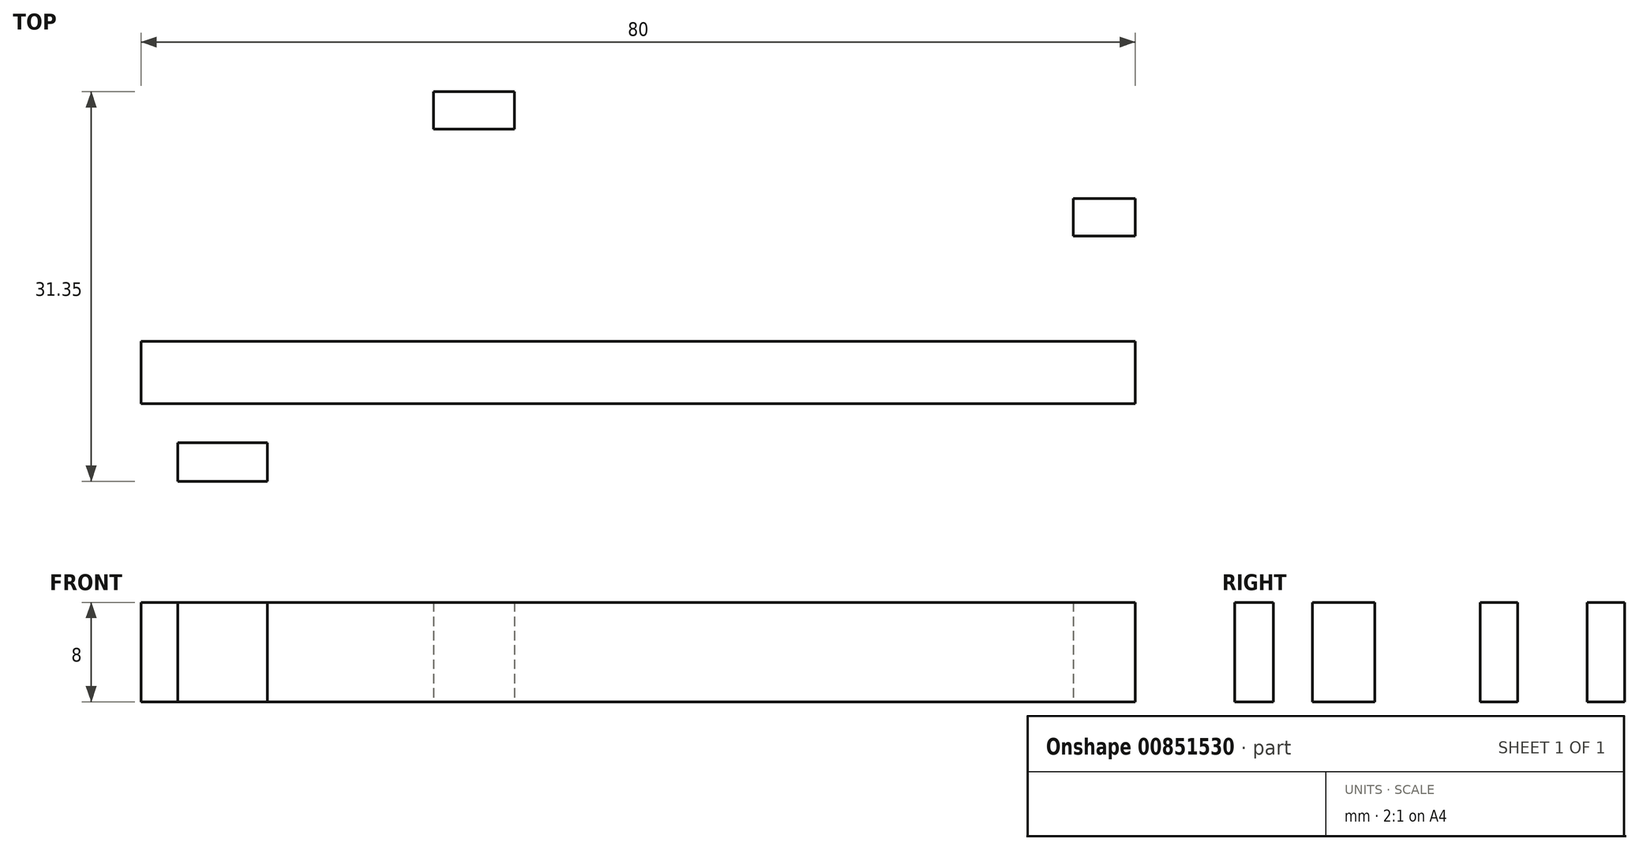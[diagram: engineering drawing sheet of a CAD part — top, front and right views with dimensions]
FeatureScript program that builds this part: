
annotation { "Feature Type Name" : "Feature", "Feature Type Description" : "" }
export const myFeature = defineFeature(function(context is Context, id is Id, definition is map)
    precondition{}
    {
        {
            var Q0;
            Q0=qCreatedBy(makeId("Top.planeOp"),FACE);
            var sketch = newSketch(context, id + "F0", { "sketchPlane" : qUnion([Q0])});
            skLineSegment(sketch, "E0.bottom", {"start": v(0, 0) * mm, "end": v(-80, 0) * mm});
            skLineSegment(sketch, "E0.top", {"start": v(0, 5) * mm, "end": v(-80, 5) * mm});
            skLineSegment(sketch, "E0.left", {"start": v(0, 0) * mm, "end": v(0, 5) * mm});
            skLineSegment(sketch, "E0.right", {"start": v(-80, 0) * mm, "end": v(-80, 5) * mm});
            skLineSegment(sketch, "E1.bottom", {"start": v(-8.1, 5) * mm, "end": v(-5, 5) * mm});
            skLineSegment(sketch, "E1.top", {"start": v(-8.1, 16.5) * mm, "end": v(-5, 16.5) * mm});
            skLineSegment(sketch, "E1.left", {"start": v(-8.1, 5) * mm, "end": v(-8.1, 16.5) * mm});
            skLineSegment(sketch, "E1.right", {"start": v(-5, 5) * mm, "end": v(-5, 16.5) * mm});
            skLineSegment(sketch, "E2.bottom", {"start": v(-5, 16.5) * mm, "end": v(0, 16.5) * mm});
            skLineSegment(sketch, "E2.top", {"start": v(-5, 13.5) * mm, "end": v(0, 13.5) * mm});
            skLineSegment(sketch, "E2.left", {"start": v(-5, 16.5) * mm, "end": v(-5, 13.5) * mm});
            skLineSegment(sketch, "E2.right", {"start": v(0, 16.5) * mm, "end": v(0, 13.5) * mm});
            skLineSegment(sketch, "E3.bottom", {"start": v(-46.3, 5) * mm, "end": v(-49.95, 5) * mm});
            skLineSegment(sketch, "E3.top", {"start": v(-46.3, 25.1) * mm, "end": v(-49.95, 25.1) * mm});
            skLineSegment(sketch, "E3.left", {"start": v(-46.3, 5) * mm, "end": v(-46.3, 25.1) * mm});
            skLineSegment(sketch, "E3.right", {"start": v(-49.95, 5) * mm, "end": v(-49.95, 25.1) * mm});
            skLineSegment(sketch, "E4.bottom", {"start": v(-49.95, 25.1) * mm, "end": v(-56.45, 25.1) * mm});
            skLineSegment(sketch, "E4.top", {"start": v(-49.95, 22.1) * mm, "end": v(-56.45, 22.1) * mm});
            skLineSegment(sketch, "E4.left", {"start": v(-49.95, 25.1) * mm, "end": v(-49.95, 22.1) * mm});
            skLineSegment(sketch, "E4.right", {"start": v(-56.45, 25.1) * mm, "end": v(-56.45, 22.1) * mm});
            skLineSegment(sketch, "E5.bottom", {"start": v(-75, 0) * mm, "end": v(-71.85, 0) * mm});
            skLineSegment(sketch, "E5.top", {"start": v(-75, -3.15) * mm, "end": v(-71.85, -3.15) * mm});
            skLineSegment(sketch, "E5.left", {"start": v(-75, 0) * mm, "end": v(-75, -3.15) * mm});
            skLineSegment(sketch, "E5.right", {"start": v(-71.85, 0) * mm, "end": v(-71.85, -3.15) * mm});
            skPoint(sketch, "E6", {"position": v(-73.42, -3.15) * mm});
            skLineSegment(sketch, "E7", {"start": v(-73.42, -3.15) * mm, "end": v(-73.42, -11) * mm, "construction": true});
            skLineSegment(sketch, "E8.bottom", {"start": v(-77.02, -3.15) * mm, "end": v(-69.82, -3.15) * mm});
            skLineSegment(sketch, "E8.top", {"start": v(-77.02, -6.25) * mm, "end": v(-69.82, -6.25) * mm});
            skLineSegment(sketch, "E8.left", {"start": v(-77.02, -3.15) * mm, "end": v(-77.02, -6.25) * mm});
            skLineSegment(sketch, "E8.right", {"start": v(-69.82, -3.15) * mm, "end": v(-69.82, -6.25) * mm});
            skPoint(sketch, "E8.middle", {"position": v(-73.42, -4.7) * mm});
            skSolve(sketch);
        }
        {
            var Q0;
            Q0=makeQuery(id+"F0.imprint","IMPRINT",FACE,{"disambiguationData":[TD([[makeQuery(id+"F0.imprint","IMPRINT",EDGE,{"derivedFrom":sQuery(id+"F0.wireOp",EDGE,"E0.bottom")}),-1.0]])]});
            var Q1;
            Q1=makeQuery(id+"F0.imprint","IMPRINT",FACE,{"disambiguationData":[TD([[makeQuery(id+"F0.imprint","IMPRINT",EDGE,{"derivedFrom":sQuery(id+"F0.wireOp",EDGE,"E3.bottom")}),-1.0]])]});
            var Q2;
            Q2=makeQuery(id+"F0.imprint","IMPRINT",FACE,{"disambiguationData":[TD([[makeQuery(id+"F0.imprint","IMPRINT",EDGE,{"derivedFrom":sQuery(id+"F0.wireOp",EDGE,"E4.bottom")}),1.0]])]});
            var Q3;
            Q3=makeQuery(id+"F0.imprint","IMPRINT",FACE,{"disambiguationData":[TD([[makeQuery(id+"F0.imprint","IMPRINT",EDGE,{"derivedFrom":sQuery(id+"F0.wireOp",EDGE,"E1.bottom")}),1.0]])]});
            var Q4;
            Q4=makeQuery(id+"F0.imprint","IMPRINT",FACE,{"disambiguationData":[TD([[makeQuery(id+"F0.imprint","IMPRINT",EDGE,{"derivedFrom":sQuery(id+"F0.wireOp",EDGE,"E2.bottom")}),-1.0]])]});
            var Q5;
            Q5=makeQuery(id+"F0.imprint","IMPRINT",FACE,{"disambiguationData":[TD([[makeQuery(id+"F0.imprint","IMPRINT",EDGE,{"derivedFrom":sQuery(id+"F0.wireOp",EDGE,"E5.bottom")}),-1.0]])]});
            var Q6;
            Q6=makeQuery(id+"F0.imprint","IMPRINT",FACE,{"disambiguationData":[TD([[makeQuery(id+"F0.imprint","IMPRINT",EDGE,{"derivedFrom":sQuery(id+"F0.wireOp",EDGE,"E8.top")}),1.0]])]});
            extrude(context, id + "F1", {"entities" : qUnion([Q0, Q1, Q2, Q3, Q4, Q5, Q6]), "depth" : 8 * mm, "offsetDistance" : 25 * mm});
        }
    });
